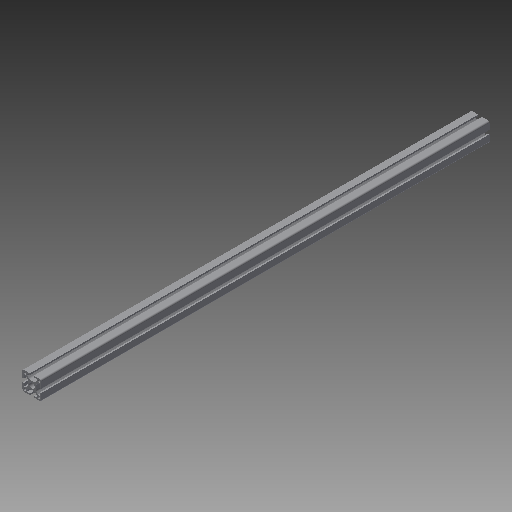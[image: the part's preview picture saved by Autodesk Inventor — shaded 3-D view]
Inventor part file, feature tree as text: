
AUTODESK INVENTOR PART (.ipt)
format: ipt  version: 2018 (Build 220112000, 112)  size: 221,184 bytes
history: native  units: mm
features: other x42, sketch x5, hole x4, extrude x1
ambient origin geometry x8: Origin, YZ Plane, XZ Plane, XY Plane, X Axis, Y Axis, Z Axis, Center Point
bodies: Solid1 (feature_tree)
feature tree (52):
  extrude  "Extrusion1"  [1 undecoded]
  hole  "Drilling 1"  [1 undecoded]
  hole  "Drilling 2"  [1 undecoded]
  hole  "Drilling 3"  [1 undecoded]
  hole  "Drilling 4"  [1 undecoded]
  other  "side_4d_XY"
  other  "side_4d_YZ"
  other  "side_4d_ZX"
  other  "side_4d_X"
  other  "side_4d_Y"
  other  "side_4d_Z"
  other  "side_4d_Center"
  other  "side_1a_XY"
  other  "side_1a_YZ"
  other  "side_1a_ZX"
  other  "side_1a_X"
  other  "side_1a_Y"
  other  "side_1a_Z"
  other  "side_1a_Center"
  other  "side_2b_XY"
  other  "side_2b_YZ"
  other  "side_2b_ZX"
  other  "side_2b_X"
  other  "side_2b_Y"
  other  "side_2b_Z"
  other  "side_2b_Center"
  other  "side_3c_XY"
  other  "side_3c_YZ"
  other  "side_3c_ZX"
  other  "side_3c_X"
  other  "side_3c_Y"
  other  "side_3c_Z"
  other  "side_3c_Center"
  other  "end_XY"
  other  "end_YZ"
  other  "end_ZX"
  other  "end_X"
  other  "end_Y"
  other  "end_Z"
  other  "end_Center"
  other  "start_XY"
  other  "start_YZ"
  other  "start_ZX"
  other  "start_X"
  other  "start_Y"
  other  "start_Z"
  other  "start_Center"
  sketch  "Skizze_1"  dims[d0=950.0mm d1=0.0mm]
  sketch  "Sketch2"  dims[d2=5.0mm d3=6.0mm d4=4.0mm d5=2.0mm d6=90.0deg d7=6000.0mm d8=0.0mm]
  sketch  "Sketch3"  dims[d9=5.0mm d10=6.0mm d11=4.0mm d12=2.0mm d13=90.0deg d14=6000.0mm d15=0.0mm]
  sketch  "Sketch4"  dims[d16=5.0mm d17=6.0mm d18=4.0mm d19=2.0mm d20=90.0deg d21=6000.0mm d22=0.0mm]
  sketch  "Sketch5"  dims[d23=5.0mm d24=6.0mm d25=4.0mm d26=2.0mm d27=90.0deg d28=6000.0mm d29=0.0mm]
note: 5 required parameter values undecoded (feature->parameter linkage not recoverable at this tier; creation-order binding heuristic only, values carry confidence <= 0.55)
